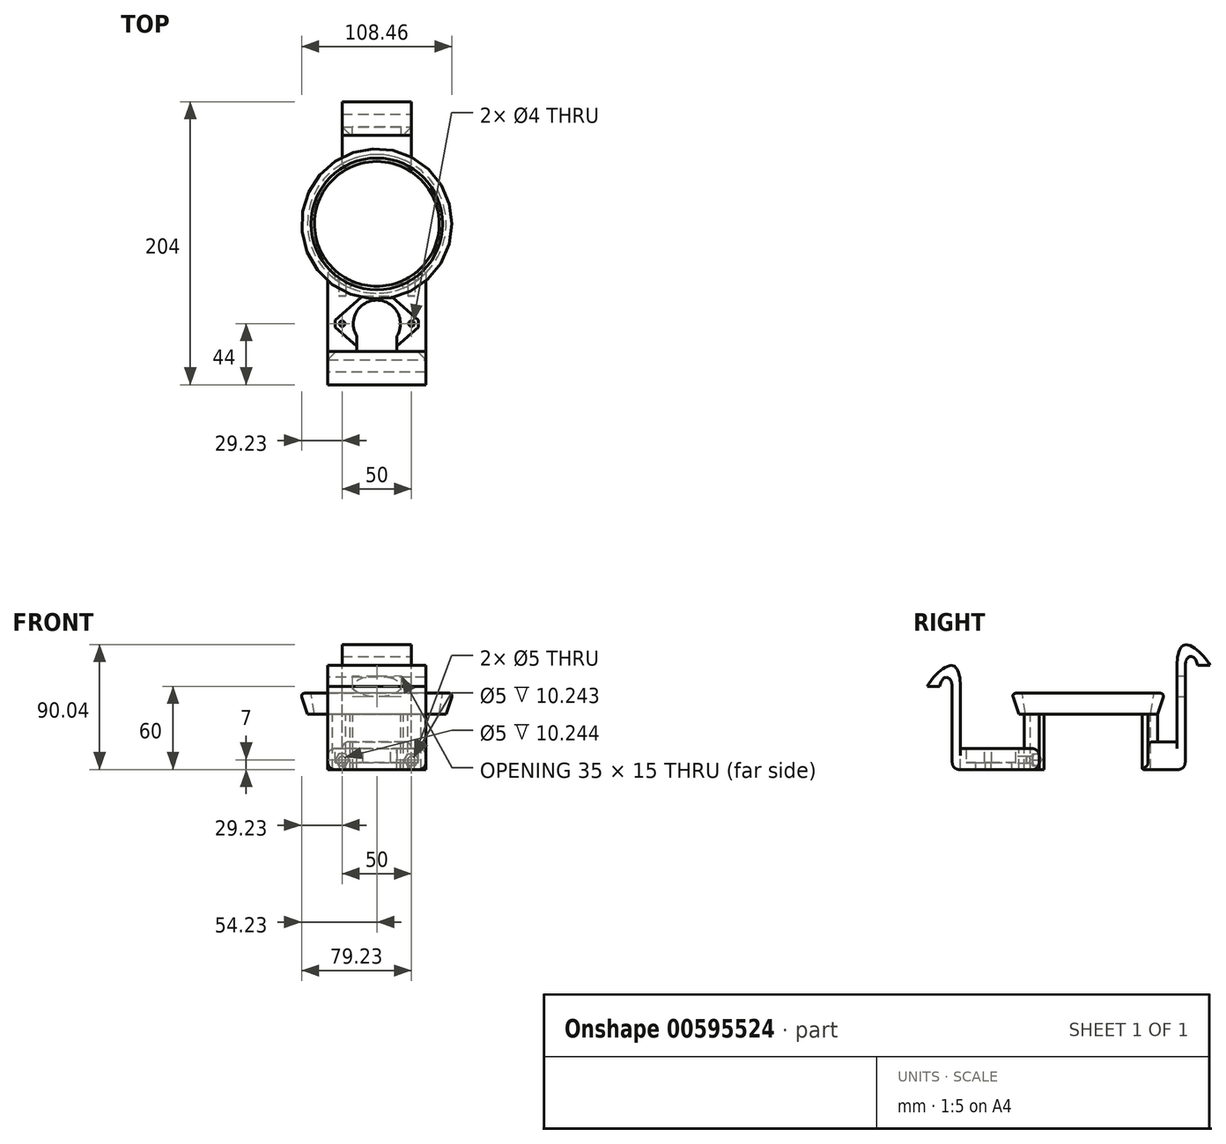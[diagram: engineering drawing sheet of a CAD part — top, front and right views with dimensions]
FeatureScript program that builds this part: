
annotation { "Feature Type Name" : "Feature", "Feature Type Description" : "" }
export const myFeature = defineFeature(function(context is Context, id is Id, definition is map)
    precondition{}
    {
        {
            var Q0;
            Q0=qCreatedBy(makeId("Top.planeOp"),FACE);
            cPlane(context, id + "F0", {"entities" : qUnion([Q0]), "cplaneType" : CPlaneType.OFFSET, "offset" : 40 * mm, "width" : 150 * mm, "height" : 150 * mm});
        }
        {
            var Q0;
            Q0=qCreatedBy(id+"F0.planeOp",FACE);
            var sketch = newSketch(context, id + "F1", { "sketchPlane" : qUnion([Q0])});
            skCircle(sketch, "E0", {"center": v(0, 0) * mm, "radius": 55 * mm});
            skSolve(sketch);
        }
        {
            var Q0;
            Q0=qCreatedBy(id+"F0.planeOp",FACE);
            cPlane(context, id + "F2", {"entities" : qUnion([Q0]), "cplaneType" : CPlaneType.OFFSET, "offset" : 15 * mm, "oppositeDirection" : true, "width" : 150 * mm, "height" : 150 * mm});
        }
        {
            var Q0;
            Q0=qCreatedBy(id+"F2.planeOp",FACE);
            var sketch = newSketch(context, id + "F3", { "sketchPlane" : qUnion([Q0])});
            skCircle(sketch, "E1", {"center": v(0, 0) * mm, "radius": 50 * mm});
            skSolve(sketch);
        }
        {
            var Q0;
            Q0=makeQuery(id+"F1.imprint","IMPRINT",FACE,{"disambiguationData":[TD([[makeQuery(id+"F1.imprint","IMPRINT",EDGE,{"derivedFrom":sQuery(id+"F1.wireOp",EDGE,"E0")}),1.0]])]});
            var Q1;
            Q1=makeQuery(id+"F3.imprint","IMPRINT",FACE,{"disambiguationData":[TD([[makeQuery(id+"F3.imprint","IMPRINT",EDGE,{"derivedFrom":sQuery(id+"F3.wireOp",EDGE,"E1")}),1.0]])]});
            loft(context, id + "F4", {"sheetProfilesArray" : [{ "sheetProfileEntities" : qUnion([Q0]) }, { "sheetProfileEntities" : qUnion([Q1]) }]});
        }
        {
            var Q0;
            Q0=makeQuery(id+"F4.opLoft","CAP_FACE",FACE,{"disambiguationData":[OSD([makeQuery(id+"F1.imprint","IMPRINT",FACE,{"disambiguationData":[TD([[makeQuery(id+"F1.imprint","IMPRINT",EDGE,{"derivedFrom":sQuery(id+"F1.wireOp",EDGE,"E0")}),1.0]])]})])],"isStart":true});
            var sketch = newSketch(context, id + "F5", { "sketchPlane" : qUnion([Q0])});
            skCircle(sketch, "E2", {"center": v(0, 0) * mm, "radius": 47.5 * mm});
            skSolve(sketch);
        }
        {
            var Q0;
            Q0=makeQuery(id+"F4.opLoft","CAP_FACE",FACE,{"disambiguationData":[OSD([makeQuery(id+"F3.imprint","IMPRINT",FACE,{"disambiguationData":[TD([[makeQuery(id+"F3.imprint","IMPRINT",EDGE,{"derivedFrom":sQuery(id+"F3.wireOp",EDGE,"E1")}),1.0]])]})])],"isStart":true});
            var sketch = newSketch(context, id + "F6", { "sketchPlane" : qUnion([Q0])});
            skCircle(sketch, "E3", {"center": v(0, 0) * mm, "radius": 45 * mm});
            skSolve(sketch);
        }
        {
            var Q1;
            Q1=makeQuery(id+"F5.imprint","IMPRINT",FACE,{"disambiguationData":[TD([[makeQuery(id+"F5.imprint","IMPRINT",EDGE,{"derivedFrom":sQuery(id+"F5.wireOp",EDGE,"E2")}),1.0]])]});
            var Q2;
            Q2=makeQuery(id+"F6.imprint","IMPRINT",FACE,{"disambiguationData":[TD([[makeQuery(id+"F6.imprint","IMPRINT",EDGE,{"derivedFrom":sQuery(id+"F6.wireOp",EDGE,"E3")}),1.0]])]});
            loft(context, id + "F7", {"operationType" : NewBodyOperationType.REMOVE, "sheetProfilesArray" : [{ "sheetProfileEntities" : qUnion([Q1]) }, { "sheetProfileEntities" : qUnion([Q2]) }]});
        }
        {
            var Q0;
            Q0=makeQuery(id+"F4.opLoft","CAP_FACE",FACE,{"disambiguationData":[OSD([makeQuery(id+"F3.imprint","IMPRINT",FACE,{"disambiguationData":[TD([[makeQuery(id+"F3.imprint","IMPRINT",EDGE,{"derivedFrom":sQuery(id+"F3.wireOp",EDGE,"E1")}),1.0]])]})])],"isStart":true});
            var sketch = newSketch(context, id + "F8", { "sketchPlane" : qUnion([Q0])});
            skArc(sketch, "E4.0", {"start": v(-25, -43.3) * mm, "mid": v(0, -50) * mm, "end": v(25, -43.3) * mm});
            skArc(sketch, "E5.0", {"start": v(-22.5, -38.97) * mm, "mid": v(0, -45) * mm, "end": v(22.5, -38.97) * mm});
            skLineSegment(sketch, "E6", {"start": v(25, -43.3) * mm, "end": v(0, 0) * mm});
            skLineSegment(sketch, "E7", {"start": v(-25, -43.3) * mm, "end": v(0, 0) * mm});
            skLineSegment(sketch, "E8", {"start": v(0, 0) * mm, "end": v(-35.36, 35.36) * mm});
            skLineSegment(sketch, "E9", {"start": v(0, 0) * mm, "end": v(35.36, 35.36) * mm});
            skArc(sketch, "E10.0", {"start": v(35.36, 35.36) * mm, "mid": v(27.78, 41.57) * mm, "end": v(19.13, 46.2) * mm});
            skArc(sketch, "E11.0", {"start": v(31.82, 31.82) * mm, "mid": v(25, 37.42) * mm, "end": v(17.22, 41.57) * mm});
            skLineSegment(sketch, "E12", {"start": v(-19.13, 46.2) * mm, "end": v(0, 0) * mm});
            skLineSegment(sketch, "E13", {"start": v(19.13, 46.2) * mm, "end": v(0, 0) * mm});
            skArc(sketch, "E14.trimOffspring", {"start": v(-17.22, 41.57) * mm, "mid": v(-25, 37.42) * mm, "end": v(-31.82, 31.82) * mm});
            skArc(sketch, "E15.trimOffspring", {"start": v(-19.13, 46.2) * mm, "mid": v(-27.78, 41.57) * mm, "end": v(-35.36, 35.36) * mm});
            skSolve(sketch);
        }
        {
            var Q0;
            {var subQ3=sQuery(id+"F8.wireOp",EDGE,"E5.0");Q0=makeQuery(id+"F8.imprint","IMPRINT",FACE,{"disambiguationData":[TD([[makeQuery(id+"F8.imprint","IMPRINT",EDGE,{"derivedFrom":subQ3}),-1.0]])]});}
            var Q1;
            {var subQ0=sQuery(id+"F8.wireOp",EDGE,"E10.0");Q1=makeQuery(id+"F8.imprint","IMPRINT",FACE,{"disambiguationData":[TD([[makeQuery(id+"F8.imprint","IMPRINT",EDGE,{"derivedFrom":subQ0}),1.0]])]});}
            var Q2;
            {var subQ3=sQuery(id+"F8.wireOp",EDGE,"E14.trimOffspring");Q2=makeQuery(id+"F8.imprint","IMPRINT",FACE,{"disambiguationData":[TD([[makeQuery(id+"F8.imprint","IMPRINT",EDGE,{"derivedFrom":subQ3}),-1.0]])]});}
            extrude(context, id + "F9", {"entities" : qUnion([Q0, Q1, Q2]), "operationType" : NewBodyOperationType.ADD, "depth" : 40 * mm, "offsetDistance" : 25 * mm});
        }
        {
            var Q0;
            Q0=qCreatedBy(makeId("Front.planeOp"),FACE);
            cPlane(context, id + "F10", {"entities" : qUnion([Q0]), "cplaneType" : CPlaneType.OFFSET, "offset" : 98 * mm, "width" : 150 * mm, "height" : 150 * mm});
        }
        {
            var Q0;
            Q0=qCreatedBy(id+"F10.planeOp",FACE);
            var sketch = newSketch(context, id + "F11", { "sketchPlane" : qUnion([Q0])});
            skLineSegment(sketch, "E16.bottom", {"start": v(-35.36, -15) * mm, "end": v(35.36, -15) * mm});
            skLineSegment(sketch, "E16.top", {"start": v(-35.36, 0) * mm, "end": v(35.36, 0) * mm});
            skLineSegment(sketch, "E16.left", {"start": v(-35.36, -15) * mm, "end": v(-35.36, 0) * mm});
            skLineSegment(sketch, "E16.right", {"start": v(35.36, -15) * mm, "end": v(35.36, 0) * mm});
            skSolve(sketch);
        }
        {
            var Q0;
            Q0=makeQuery(id+"F11.imprint","IMPRINT",FACE,{"disambiguationData":[TD([[makeQuery(id+"F11.imprint","IMPRINT",EDGE,{"derivedFrom":sQuery(id+"F11.wireOp",EDGE,"E16.bottom")}),1.0]])]});
            var Q1;
            Q1=makeQuery(id+"F9.opExtrude","SWEPT_FACE",FACE,{"disambiguationData":[OSD([sQuery(id+"F8.wireOp",EDGE,"E10.0")])]});
            extrude(context, id + "F12", {"entities" : qUnion([Q0]), "endBound" : BoundingType.UP_TO_SURFACE, "oppositeDirection" : true, "depth" : 25 * mm, "endBoundEntityFace" : qUnion([Q1]), "offsetDistance" : 25 * mm});
        }
        {
            var Q0;
            Q0=makeQuery(id+"F12.opExtrude","SWEPT_FACE",FACE,{"disambiguationData":[OSD([sQuery(id+"F11.wireOp",EDGE,"E16.top")])]});
            var sketch = newSketch(context, id + "F13", { "sketchPlane" : qUnion([Q0])});
            skCircle(sketch, "E17", {"center": v(0, -72) * mm, "radius": 17 * mm});
            skLineSegment(sketch, "E18.bottom", {"start": v(-14.5, -92) * mm, "end": v(14.5, -92) * mm});
            skLineSegment(sketch, "E18.top", {"start": v(-14.5, -78.53) * mm, "end": v(14.5, -78.53) * mm});
            skLineSegment(sketch, "E18.left", {"start": v(-14.5, -92) * mm, "end": v(-14.5, -78.53) * mm});
            skLineSegment(sketch, "E18.right", {"start": v(14.5, -92) * mm, "end": v(14.5, -78.53) * mm});
            skPoint(sketch, "E18.middle", {"position": v(0, -85.27) * mm});
            skSolve(sketch);
        }
        {
            var Q0;
            Q0 = qSketchRegion(id + "F13", true);
            extrude(context, id + "F14", {"entities" : qUnion([Q0]), "operationType" : NewBodyOperationType.REMOVE, "oppositeDirection" : true, "depth" : 25 * mm, "offsetDistance" : 25 * mm});
        }
        {
            var Q0;
            Q0=makeQuery(id+"F12.opExtrude","SWEPT_FACE",FACE,{"disambiguationData":[OSD([sQuery(id+"F11.wireOp",EDGE,"E16.top")])]});
            var sketch = newSketch(context, id + "F15", { "sketchPlane" : qUnion([Q0])});
            skLineSegment(sketch, "E19.bottom", {"start": v(-10, -92) * mm, "end": v(10, -92) * mm});
            skLineSegment(sketch, "E19.top", {"start": v(-10, -52) * mm, "end": v(10, -52) * mm});
            skLineSegment(sketch, "E19.left", {"start": v(-10, -92) * mm, "end": v(-10, -52) * mm, "construction": true});
            skLineSegment(sketch, "E19.right", {"start": v(10, -92) * mm, "end": v(10, -52) * mm, "construction": true});
            skPoint(sketch, "E19.middle", {"position": v(0, -72) * mm});
            skLineSegment(sketch, "E20.bottom", {"start": v(-30, -74.5) * mm, "end": v(30, -74.5) * mm, "construction": true});
            skLineSegment(sketch, "E20.top", {"start": v(-30, -69.5) * mm, "end": v(30, -69.5) * mm, "construction": true});
            skLineSegment(sketch, "E20.left", {"start": v(-30, -74.5) * mm, "end": v(-30, -69.5) * mm});
            skLineSegment(sketch, "E20.right", {"start": v(30, -74.5) * mm, "end": v(30, -69.5) * mm});
            skLineSegment(sketch, "E21", {"start": v(-30, -74.5) * mm, "end": v(-10, -92) * mm});
            skLineSegment(sketch, "E22", {"start": v(10, -92) * mm, "end": v(30, -74.5) * mm});
            skLineSegment(sketch, "E23", {"start": v(10, -52) * mm, "end": v(30, -69.5) * mm});
            skLineSegment(sketch, "E24", {"start": v(-30, -69.5) * mm, "end": v(-10, -52) * mm});
            skSolve(sketch);
        }
        {
            var Q0;
            Q0=makeQuery(id+"F15.imprint","IMPRINT",FACE,{"disambiguationData":[TD([[makeQuery(id+"F15.imprint","IMPRINT",EDGE,{"derivedFrom":sQuery(id+"F15.wireOp",EDGE,"E19.bottom")}),1.0]])]});
            var Q1;
            Q1=makeQuery(id+"F15.imprint","IMPRINT",FACE,{"disambiguationData":[TD([[makeQuery(id+"F15.imprint","IMPRINT",EDGE,{"derivedFrom":sQuery(id+"F15.wireOp",EDGE,"E19.top")}),-1.0]])]});
            extrude(context, id + "F16", {"entities" : qUnion([Q0, Q1]), "operationType" : NewBodyOperationType.REMOVE, "oppositeDirection" : true, "depth" : 10 * mm, "offsetDistance" : 25 * mm});
        }
        {
            var Q0;
            Q0=makeQuery(id+"F16.boolean.opBoolean","COPY",FACE,{"derivedFrom":makeQuery(id+"F16.opExtrude","CAP_FACE",FACE,{"disambiguationData":[OSD([sQuery(id+"F13.wireOp",EDGE,"E17"),sQuery(id+"F15.wireOp",EDGE,"E19.bottom"),sQuery(id+"F15.wireOp",EDGE,"E19.top"),sQuery(id+"F15.wireOp",EDGE,"E20.left"),sQuery(id+"F15.wireOp",EDGE,"E20.right"),sQuery(id+"F15.wireOp",EDGE,"E21"),sQuery(id+"F15.wireOp",EDGE,"E22"),sQuery(id+"F15.wireOp",EDGE,"E23"),sQuery(id+"F15.wireOp",EDGE,"E24")])],"isStart":false})});
            var sketch = newSketch(context, id + "F17", { "sketchPlane" : qUnion([Q0])});
            skLineSegment(sketch, "E25", {"start": v(0, -115) * mm, "end": v(0, -52) * mm, "construction": true});
            skCircle(sketch, "E26", {"center": v(-25, -72) * mm, "radius": 2 * mm});
            skLineSegment(sketch, "E27", {"start": v(30, -72) * mm, "end": v(-30, -72) * mm, "construction": true});
            skCircle(sketch, "E28", {"center": v(25, -72) * mm, "radius": 2 * mm});
            skSolve(sketch);
        }
        {
            var Q0;
            Q0 = qSketchRegion(id + "F17", true);
            extrude(context, id + "F18", {"entities" : qUnion([Q0]), "operationType" : NewBodyOperationType.REMOVE, "oppositeDirection" : true, "depth" : 25 * mm, "offsetDistance" : 25 * mm});
        }
        {
            var Q0;
            Q0=makeQuery(id+"F12.opExtrude","SWEPT_FACE",FACE,{"disambiguationData":[OSD([sQuery(id+"F11.wireOp",EDGE,"E16.left")])]});
            var sketch = newSketch(context, id + "F19", { "sketchPlane" : qUnion([Q0])});
            skLineSegment(sketch, "E29.bottom", {"start": v(98, 0) * mm, "end": v(92, 0) * mm});
            skLineSegment(sketch, "E29.top", {"start": v(98, 45) * mm, "end": v(92, 45) * mm});
            skLineSegment(sketch, "E29.left", {"start": v(98, 0) * mm, "end": v(98, 45) * mm});
            skLineSegment(sketch, "E29.right", {"start": v(92, 0) * mm, "end": v(92, 45) * mm});
            skFitSpline(sketch, "E30", {"points": [v(92, 45) * mm, v(98, 60) * mm, v(116, 45) * mm], "startDerivative": vector(1.74, 50.26) * mm, "endDerivative": vector(20.6, -39.42) * mm});
            skLineSegment(sketch, "E31", {"start": v(107, 45) * mm, "end": v(116, 45) * mm});
            skFitSpline(sketch, "E32", {"points": [v(98, 45) * mm, v(102.5, 51.43) * mm, v(107, 45) * mm], "startDerivative": vector(1.65, 31.69) * mm, "endDerivative": vector(7.44, -28.03) * mm});
            skSolve(sketch);
        }
        {
            var Q0;
            Q0 = qSketchRegion(id + "F19", true);
            var Q1;
            Q1=makeQuery(id+"F12.opExtrude","SWEPT_FACE",FACE,{"disambiguationData":[OSD([sQuery(id+"F11.wireOp",EDGE,"E16.right")])]});
            extrude(context, id + "F20", {"entities" : qUnion([Q0]), "operationType" : NewBodyOperationType.ADD, "endBound" : BoundingType.UP_TO_SURFACE, "oppositeDirection" : true, "depth" : 25 * mm, "endBoundEntityFace" : qUnion([Q1]), "offsetDistance" : 25 * mm});
        }
        {
            var Q0;
            Q0=qCreatedBy(makeId("Front.planeOp"),FACE);
            cPlane(context, id + "F21", {"entities" : qUnion([Q0]), "cplaneType" : CPlaneType.OFFSET, "offset" : 70 * mm, "oppositeDirection" : true, "width" : 150 * mm, "height" : 150 * mm});
        }
        {
            var Q0;
            Q0=qCreatedBy(id+"F21.planeOp",FACE);
            var sketch = newSketch(context, id + "F22", { "sketchPlane" : qUnion([Q0])});
            skLineSegment(sketch, "E33.bottom", {"start": v(-25, -15) * mm, "end": v(25, -15) * mm});
            skLineSegment(sketch, "E33.top", {"start": v(-25, 5) * mm, "end": v(25, 5) * mm});
            skLineSegment(sketch, "E33.left", {"start": v(-25, -15) * mm, "end": v(-25, 5) * mm});
            skLineSegment(sketch, "E33.right", {"start": v(25, -15) * mm, "end": v(25, 5) * mm});
            skSolve(sketch);
        }
        {
            var Q0;
            Q0=makeQuery(id+"F22.imprint","IMPRINT",FACE,{"disambiguationData":[TD([[makeQuery(id+"F22.imprint","IMPRINT",EDGE,{"derivedFrom":sQuery(id+"F22.wireOp",EDGE,"E33.bottom")}),1.0]])]});
            var Q1;
            Q1=makeQuery(id+"F9.opExtrude","SWEPT_FACE",FACE,{"disambiguationData":[OSD([sQuery(id+"F8.wireOp",EDGE,"E4.0")])]});
            extrude(context, id + "F23", {"entities" : qUnion([Q0]), "operationType" : NewBodyOperationType.ADD, "endBound" : BoundingType.UP_TO_SURFACE, "depth" : 25 * mm, "endBoundEntityFace" : qUnion([Q1]), "offsetDistance" : 25 * mm});
        }
        {
            var Q0;
            Q0=makeQuery(id+"F23.opExtrude","SWEPT_FACE",FACE,{"disambiguationData":[OSD([sQuery(id+"F22.wireOp",EDGE,"E33.right")])]});
            var sketch = newSketch(context, id + "F24", { "sketchPlane" : qUnion([Q0])});
            skLineSegment(sketch, "E34.bottom", {"start": v(70, 5) * mm, "end": v(64, 5) * mm});
            skLineSegment(sketch, "E34.top", {"start": v(70, 60) * mm, "end": v(64, 60) * mm});
            skLineSegment(sketch, "E34.left", {"start": v(70, 5) * mm, "end": v(70, 60) * mm});
            skLineSegment(sketch, "E34.right", {"start": v(64, 5) * mm, "end": v(64, 60) * mm});
            skFitSpline(sketch, "E35", {"points": [v(64, 60) * mm, v(70, 75) * mm, v(88, 60) * mm], "startDerivative": vector(1.74, 50.26) * mm, "endDerivative": vector(20.6, -39.42) * mm});
            skLineSegment(sketch, "E36", {"start": v(79, 60) * mm, "end": v(88, 60) * mm});
            skFitSpline(sketch, "E37", {"points": [v(70, 60) * mm, v(74.5, 66.6) * mm, v(79, 60) * mm], "startDerivative": vector(1.65, 31.69) * mm, "endDerivative": vector(7.44, -28.03) * mm});
            skSolve(sketch);
        }
        {
            var Q0;
            Q0 = qSketchRegion(id + "F24", true);
            var Q1;
            Q1=makeQuery(id+"F23.opExtrude","SWEPT_FACE",FACE,{"disambiguationData":[OSD([sQuery(id+"F22.wireOp",EDGE,"E33.left")])]});
            extrude(context, id + "F25", {"entities" : qUnion([Q0]), "operationType" : NewBodyOperationType.ADD, "endBound" : BoundingType.UP_TO_SURFACE, "oppositeDirection" : true, "depth" : 25 * mm, "endBoundEntityFace" : qUnion([Q1]), "offsetDistance" : 25 * mm});
        }
        {
            var Q0;
            Q0=makeQuery(id+"F25.boolean.opBoolean","MERGE",FACE,{"derivedFrom":[makeQuery(id+"F23.opExtrude","CAP_FACE",FACE,{"disambiguationData":[OSD([sQuery(id+"F22.wireOp",EDGE,"E33.bottom"),sQuery(id+"F22.wireOp",EDGE,"E33.top"),sQuery(id+"F22.wireOp",EDGE,"E33.left"),sQuery(id+"F22.wireOp",EDGE,"E33.right")])],"isStart":true}),makeQuery(id+"F25.opExtrude","SWEPT_FACE",FACE,{"disambiguationData":[OSD([sQuery(id+"F24.wireOp",EDGE,"E34.left")])]})]});
            var sketch = newSketch(context, id + "F26", { "sketchPlane" : qUnion([Q0])});
            skEllipse(sketch, "E38", {"center": v(0, 45) * mm, "majorRadius": 17.5 * mm, "minorRadius": 7.5 * mm, "majorAxis": v(-1, 0)});
            skSolve(sketch);
        }
        {
            var Q0;
            {var subQ0=sQuery(id+"F26.wireOp",EDGE,"E38");var subQ1=makeQuery(id+"F25.opExtrude","SWEPT_EDGE",EDGE,{"disambiguationData":[OSD([sQuery(id+"F24.wireOp",EDGE,"E34.top"),sQuery(id+"F24.wireOp",EDGE,"E34.left"),sQuery(id+"F24.wireOp",EDGE,"E37")])]});var subQ2=makeQuery(id+"F26.imprint","INTERSECT",VERTEX,{"disambiguationData":[OD(0.0)],"derivedFrom":[subQ1,subQ0]});Q0=makeQuery(id+"F26.imprint","IMPRINT",FACE,{"disambiguationData":[TD([[makeQuery(id+"F26.imprint","IMPRINT",EDGE,{"disambiguationData":[TD([[subQ2,1.0]])],"derivedFrom":subQ0}),1.0]])]});}
            var Q1;
            Q1=sQuery(id+"F26.wireOp",EDGE,"E38");
            extrude(context, id + "F27", {"entities" : qUnion([Q0]), "operationType" : NewBodyOperationType.REMOVE, "surfaceEntities" : qUnion([Q1]), "endBound" : BoundingType.UP_TO_NEXT, "oppositeDirection" : true, "depth" : 25 * mm, "offsetDistance" : 25 * mm});
        }
        {
            var Q0;
            Q0=makeQuery(id+"F12.opExtrude","SWEPT_EDGE",EDGE,{"disambiguationData":[OSD([sQuery(id+"F11.wireOp",EDGE,"E16.top"),sQuery(id+"F11.wireOp",EDGE,"E16.right")])]});
            var Q1;
            Q1=makeQuery(id+"F12.opExtrude","SWEPT_EDGE",EDGE,{"disambiguationData":[OSD([sQuery(id+"F11.wireOp",EDGE,"E16.top"),sQuery(id+"F11.wireOp",EDGE,"E16.left")])]});
            var Q2;
            Q2=makeQuery(id+"F20.opExtrude","SWEPT_EDGE",EDGE,{"disambiguationData":[OSD([sQuery(id+"F11.wireOp",EDGE,"E16.top"),sQuery(id+"F11.wireOp",EDGE,"E16.left"),sQuery(id+"F19.wireOp",EDGE,"E29.bottom"),sQuery(id+"F19.wireOp",EDGE,"E29.right")])]});
            var Q3;
            Q3=makeQuery(id+"F12.opExtrude","CAP_EDGE",EDGE,{"disambiguationData":[OSD([sQuery(id+"F11.wireOp",EDGE,"E16.bottom")])],"isStart":true});
            var Q4;
            Q4=makeQuery(id+"F12.opExtrude","SWEPT_EDGE",EDGE,{"disambiguationData":[OSD([sQuery(id+"F11.wireOp",EDGE,"E16.bottom"),sQuery(id+"F11.wireOp",EDGE,"E16.left")])]});
            var Q5;
            Q5=makeQuery(id+"F12.opExtrude","SWEPT_EDGE",EDGE,{"disambiguationData":[OSD([sQuery(id+"F11.wireOp",EDGE,"E16.bottom"),sQuery(id+"F11.wireOp",EDGE,"E16.right")])]});
            fillet(context, id + "F28", {"entities" : qUnion([Q0, Q1, Q2, Q3, Q4, Q5]), "radius" : 5 * mm, "tangentPropagation" : true, "allowEdgeOverflow" : false});
        }
        {
            var Q0;
            Q0=makeQuery(id+"F23.opExtrude","SWEPT_EDGE",EDGE,{"disambiguationData":[OSD([sQuery(id+"F22.wireOp",EDGE,"E33.top"),sQuery(id+"F22.wireOp",EDGE,"E33.left")])]});
            var Q1;
            Q1=makeQuery(id+"F23.opExtrude","SWEPT_EDGE",EDGE,{"disambiguationData":[OSD([sQuery(id+"F22.wireOp",EDGE,"E33.top"),sQuery(id+"F22.wireOp",EDGE,"E33.right")])]});
            var Q2;
            Q2=makeQuery(id+"F25.opExtrude","SWEPT_EDGE",EDGE,{"disambiguationData":[OSD([sQuery(id+"F22.wireOp",EDGE,"E33.top"),sQuery(id+"F22.wireOp",EDGE,"E33.right"),sQuery(id+"F24.wireOp",EDGE,"E34.bottom"),sQuery(id+"F24.wireOp",EDGE,"E34.right")])]});
            var Q3;
            Q3=makeQuery(id+"F23.opExtrude","SWEPT_EDGE",EDGE,{"disambiguationData":[OSD([sQuery(id+"F22.wireOp",EDGE,"E33.bottom"),sQuery(id+"F22.wireOp",EDGE,"E33.left")])]});
            var Q4;
            Q4=makeQuery(id+"F23.opExtrude","CAP_EDGE",EDGE,{"disambiguationData":[OSD([sQuery(id+"F22.wireOp",EDGE,"E33.bottom")])],"isStart":true});
            var Q5;
            Q5=makeQuery(id+"F23.opExtrude","SWEPT_EDGE",EDGE,{"disambiguationData":[OSD([sQuery(id+"F22.wireOp",EDGE,"E33.bottom"),sQuery(id+"F22.wireOp",EDGE,"E33.right")])]});
            fillet(context, id + "F29", {"entities" : qUnion([Q0, Q1, Q2, Q3, Q4, Q5]), "radius" : 5 * mm, "tangentPropagation" : true, "allowEdgeOverflow" : false});
        }
        {
            var Q0;
            Q0=makeQuery(id+"F4.opLoft","MID_CAP_EDGE",EDGE,{"disambiguationData":[OSD([sQuery(id+"F1.wireOp",EDGE,"E0")])],"capPos":0.0});
            fillet(context, id + "F30", {"entities" : qUnion([Q0]), "radius" : 2 * mm, "tangentPropagation" : true, "allowEdgeOverflow" : false});
        }
        {
            var Q0;
            Q0=makeQuery(id+"F16.boolean.opBoolean","COPY",FACE,{"derivedFrom":makeQuery(id+"F16.opExtrude","SWEPT_FACE",FACE,{"disambiguationData":[OSD([sQuery(id+"F15.wireOp",EDGE,"E19.top")])]})});
            cPlane(context, id + "F31", {"entities" : qUnion([Q0]), "cplaneType" : CPlaneType.OFFSET, "offset" : 0 * mm, "width" : 150 * mm, "height" : 150 * mm});
        }
        {
            var Q0;
            Q0=qCreatedBy(id+"F31.planeOp",FACE);
            var sketch = newSketch(context, id + "F32", { "sketchPlane" : qUnion([Q0])});
            skLineSegment(sketch, "E39", {"start": v(0, 235.01) * mm, "end": v(0, -10.77) * mm, "construction": true});
            skLineSegment(sketch, "E40", {"start": v(-35.37, -8) * mm, "end": v(35.4, -8) * mm, "construction": true});
            skCircle(sketch, "E41", {"center": v(-25, -8) * mm, "radius": 2.5 * mm});
            skCircle(sketch, "E42", {"center": v(25, -8) * mm, "radius": 2.5 * mm});
            skSolve(sketch);
        }
        {
            var Q0;
            Q0 = qSketchRegion(id + "F32", true);
            var Q1;
            Q1=makeQuery(id+"F9.opExtrude","SWEPT_FACE",FACE,{"disambiguationData":[OSD([sQuery(id+"F8.wireOp",EDGE,"E14.trimOffspring")])]});
            extrude(context, id + "F33", {"entities" : qUnion([Q0]), "operationType" : NewBodyOperationType.REMOVE, "oppositeDirection" : true, "depth" : 25 * mm, "endBoundEntityFace" : qUnion([Q1]), "offsetDistance" : 25 * mm});
        }
        {
            var Q0;
            Q0=makeQuery(id+"F9.opExtrude","SWEPT_EDGE",EDGE,{"disambiguationData":[OSD([sQuery(id+"F1.wireOp",EDGE,"E0"),sQuery(id+"F3.wireOp",EDGE,"E1"),sQuery(id+"F8.wireOp",EDGE,"E10.0"),sQuery(id+"F8.wireOp",EDGE,"E13")])]});
            var Q1;
            Q1=makeQuery(id+"F9.opExtrude","SWEPT_EDGE",EDGE,{"disambiguationData":[OSD([sQuery(id+"F1.wireOp",EDGE,"E0"),sQuery(id+"F3.wireOp",EDGE,"E1"),sQuery(id+"F8.wireOp",EDGE,"E12"),sQuery(id+"F8.wireOp",EDGE,"E15.trimOffspring")])]});
            cPlane(context, id + "F34", {"entities" : qUnion([Q0, Q1]), "cplaneType" : CPlaneType.LINE_ANGLE, "offset" : 25 * mm, "angle" : 0 * degree, "width" : 150 * mm, "height" : 150 * mm});
        }
        {
            var Q0;
            Q0=qCreatedBy(id+"F34.planeOp",FACE);
            cPlane(context, id + "F35", {"entities" : qUnion([Q0]), "cplaneType" : CPlaneType.OFFSET, "offset" : 10 * mm, "oppositeDirection" : true, "width" : 150 * mm, "height" : 150 * mm});
        }
        {
            var Q0;
            Q0=qCreatedBy(id+"F35.planeOp",FACE);
            var sketch = newSketch(context, id + "F36", { "sketchPlane" : qUnion([Q0])});
            skCircle(sketch, "E43", {"center": v(25, -8) * mm, "radius": 5 * mm, "construction": true});
            skLineSegment(sketch, "E44.0", {"start": v(27.5, -3.67) * mm, "end": v(30, -8) * mm});
            skLineSegment(sketch, "E44.1", {"start": v(30, -8) * mm, "end": v(27.5, -12.33) * mm});
            skLineSegment(sketch, "E44.2", {"start": v(27.5, -12.33) * mm, "end": v(22.5, -12.33) * mm});
            skLineSegment(sketch, "E44.3", {"start": v(22.5, -12.33) * mm, "end": v(20, -8) * mm});
            skLineSegment(sketch, "E44.4", {"start": v(20, -8) * mm, "end": v(22.5, -3.67) * mm});
            skLineSegment(sketch, "E44.5", {"start": v(22.5, -3.67) * mm, "end": v(27.5, -3.67) * mm});
            skLineSegment(sketch, "E45", {"start": v(0, 12.18) * mm, "end": v(0, -15.3) * mm, "construction": true});
            skCircle(sketch, "E46", {"center": v(-25, -8) * mm, "radius": 5 * mm, "construction": true});
            skLineSegment(sketch, "E47.MirrorCS", {"start": v(-22.5, -12.33) * mm, "end": v(-20, -8) * mm});
            skLineSegment(sketch, "E48.MirrorCS", {"start": v(-20, -8) * mm, "end": v(-22.5, -3.67) * mm});
            skLineSegment(sketch, "E49.MirrorCS", {"start": v(-30, -8) * mm, "end": v(-27.5, -12.33) * mm});
            skLineSegment(sketch, "E50.MirrorCS", {"start": v(-27.5, -12.33) * mm, "end": v(-22.5, -12.33) * mm});
            skLineSegment(sketch, "E51.MirrorCS", {"start": v(-22.5, -3.67) * mm, "end": v(-27.5, -3.67) * mm});
            skLineSegment(sketch, "E52.MirrorCS", {"start": v(-27.5, -3.67) * mm, "end": v(-30, -8) * mm});
            skSolve(sketch);
        }
        {
            var Q0;
            Q0 = qSketchRegion(id + "F36", true);
            extrude(context, id + "F37", {"entities" : qUnion([Q0]), "operationType" : NewBodyOperationType.REMOVE, "depth" : 4 * mm, "offsetDistance" : 25 * mm, "hasSecondDirection" : true, "secondDirectionOppositeDirection" : true, "secondDirectionDepth" : 3 * mm});
        }
    });
